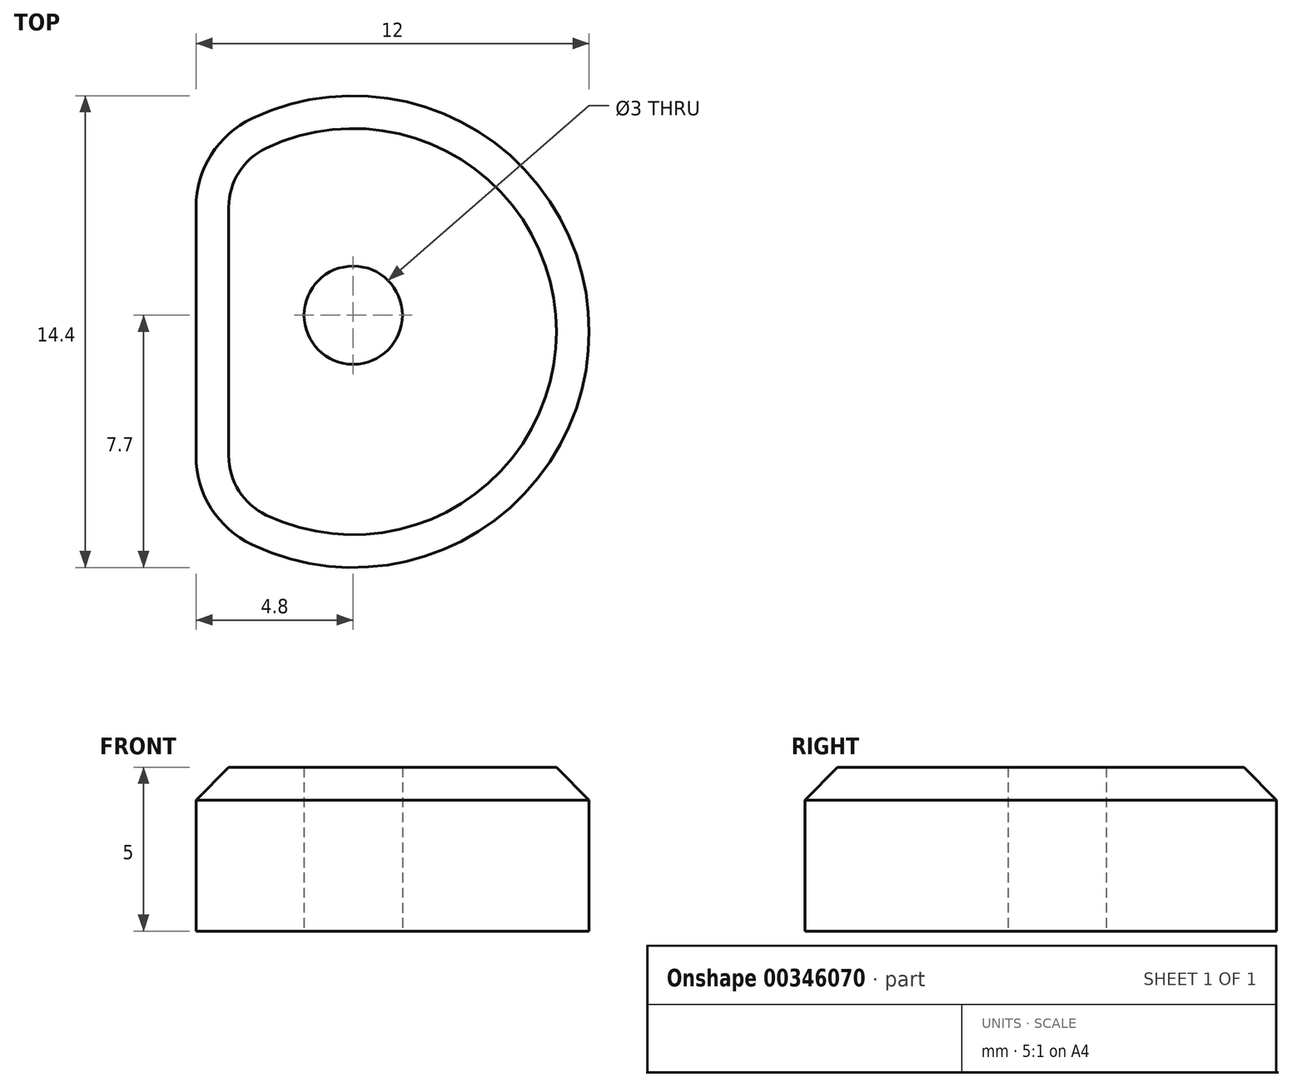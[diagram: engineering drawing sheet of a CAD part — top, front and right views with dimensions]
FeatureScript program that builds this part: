
annotation { "Feature Type Name" : "Feature", "Feature Type Description" : "" }
export const myFeature = defineFeature(function(context is Context, id is Id, definition is map)
    precondition{}
    {
        {
            var Q0;
            Q0=qCreatedBy(makeId("Top.planeOp"),FACE);
            var sketch = newSketch(context, id + "F0", { "sketchPlane" : qUnion([Q0])});
            skCircle(sketch, "E0", {"center": v(0, 0) * mm, "radius": 1.5 * mm});
            skLineSegment(sketch, "E1", {"start": v(0, 0) * mm, "end": v(0, -0.5) * mm, "construction": true});
            skArc(sketch, "E2", {"start": v(-3.09, -7) * mm, "mid": v(7.2, -0.5) * mm, "end": v(-3.09, 6) * mm});
            skLineSegment(sketch, "E3", {"start": v(-4.8, 3.3) * mm, "end": v(-4.8, -4.3) * mm});
            skPoint(sketch, "E4.visualSharp", {"position": v(-4.8, 4.87) * mm});
            skArc(sketch, "E4.filletArc", {"start": v(-3.09, 6) * mm, "mid": v(-4.34, 4.9) * mm, "end": v(-4.8, 3.3) * mm});
            skPoint(sketch, "E5.visualSharp", {"position": v(-4.8, -5.87) * mm});
            skArc(sketch, "E5.filletArc", {"start": v(-4.8, -4.3) * mm, "mid": v(-4.34, -5.9) * mm, "end": v(-3.09, -7) * mm});
            skSolve(sketch);
        }
        {
            var Q0;
            Q0 = qSketchRegion(id + "F0", true);
            extrude(context, id + "F1", {"entities" : qUnion([Q0]), "depth" : 5 * mm});
        }
        {
            var Q0;
            Q0=makeQuery(id+"F1.opExtrude","CAP_EDGE",EDGE,{"disambiguationData":[OSD([sQuery(id+"F0.wireOp",EDGE,"E2")])],"isStart":false});
            chamfer(context, id + "F2", {"entities" : qUnion([Q0]), "width" : 1 * mm, "tangentPropagation" : true});
        }
    });
